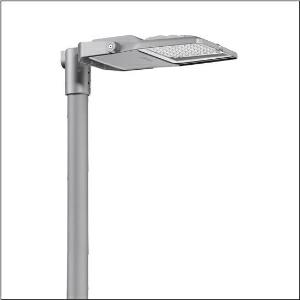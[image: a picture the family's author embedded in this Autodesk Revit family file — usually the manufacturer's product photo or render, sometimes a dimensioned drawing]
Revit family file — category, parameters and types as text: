
# Revit family: floodlight_fl_21_mini___pl33t_5xa7776d2f3a_276e
name_source: partatom
category: Lighting Fixtures
units: mm (PartAtom-declared; Revit-internal decimal feet)

## family parameters
Cut with Voids When Loaded = No
Host = Face
Light Source = No
Part Type = Normal
Room Calculation Point = No
Round Connector Dimension = Use Diameter
Shared = No

## types (1)
- --- (1 x LED, 17630 lm, 142.9 W, 3000K)
    Apparent Load = 143 VA
    CIE Flux Codes = 26 75 99 100 100
    Color Rendering = 70
    Color Temperature = 3000K
    Default Elevation = 1800 mm
    Description = Floodlight FL 21 mini, floodlight, primary light control with lens, of PMMA, primary optical cover: protective disc, of toughened safety glass, transparent, light distribution: PL33T, light emission: direct distribution, installation type: surface-mounted, LED, High Power LED, rated luminous flux: 17.630lm, luminous efficacy: 123lm/W, light colour: 730, colour temperature: 3000K, control: flexible luminous flux parameterisation, time-dependent luminous flux control, constant luminous flux control, overheat protection, pre-setting: logarithmic dimming characteristic, with terminal, 6-pole, mains connection: 220..240V, AC, 50/60Hz, start of lifetime: 143W, end of service life: 151W, reduction: 63W, luminaire housing, of diecast aluminium, powder-coated, Siteco® metallic grey (DB 702S), corrosivity category C5 mid according to DIN EN ISO 12944, sealing non-destructively replaceable, please order mast flange separately, mast bracket, of steel, galvanised, powder-coated, Siteco® metallic grey (DB 702S), Smart Interface below and above, protection rating (complete): IP66, insulation class (complete): insulation class II (safety insulation), certification: CE, ENEC, VDE, protection symbol: D, impact resistance: IK08, permissible operating ambient temperature: -40..+40°C, permissible operating ambient temperature for outdoor applications: -40..+50°C, standard: DIN EN 12944, LABS conformity tested according to VDMA 24364:2018-05, packaging unit: 1 piece

Light Distribution: PL33T
    Height = 70 mm
    Lamp = 1 x LED
    Lamp Light Flux = 17630 lm
    Lamp Power = 142.9 W
    Lamp count = 1
    Length = 485 mm
    Luminous efficacy = 123 lm/W
    Manufacturer = Siteco
    ModVariant = No
    Model = 5XA7776D2F3A
    Number of Poles = 1
    OnlyDefault = Yes
    Power Factor = 1
    Product Name = Floodlight FL 21 mini | PL33T
    Product group = floodlight | pylon annexe
    ProductGroupID = 6200
    Protection Class = Protection class II
    Protection Degree = IP 66
    RLX_Detail_Level = 1
    RLX_Emergency_Light_Flux = 0 lm
    RLX_Emergency_Type = 0
    RLX_Emergency_Type_DB = No
    RlxData = <blob elided: 100993 chars, md5=b05997d7>
    Socket = socket
    Standby Power = 0 W
    System Light Flux = 17630 lm
    System Power = 143 W
    Type Comments = factory setting: luminous flux: 100 % | dim-lin: 254 | 730 mA
    Type Image = l_1007125.jpg
    URL = http://relux.com
    VarID = @adj_118667
    Voltage = 0 V
    Weight = 0.00 kg
    Width = 337 mm

## geometry (parser evidence)
native form markers: Blend x4, Sweep x13
no freeform markers — native parametric forms only
